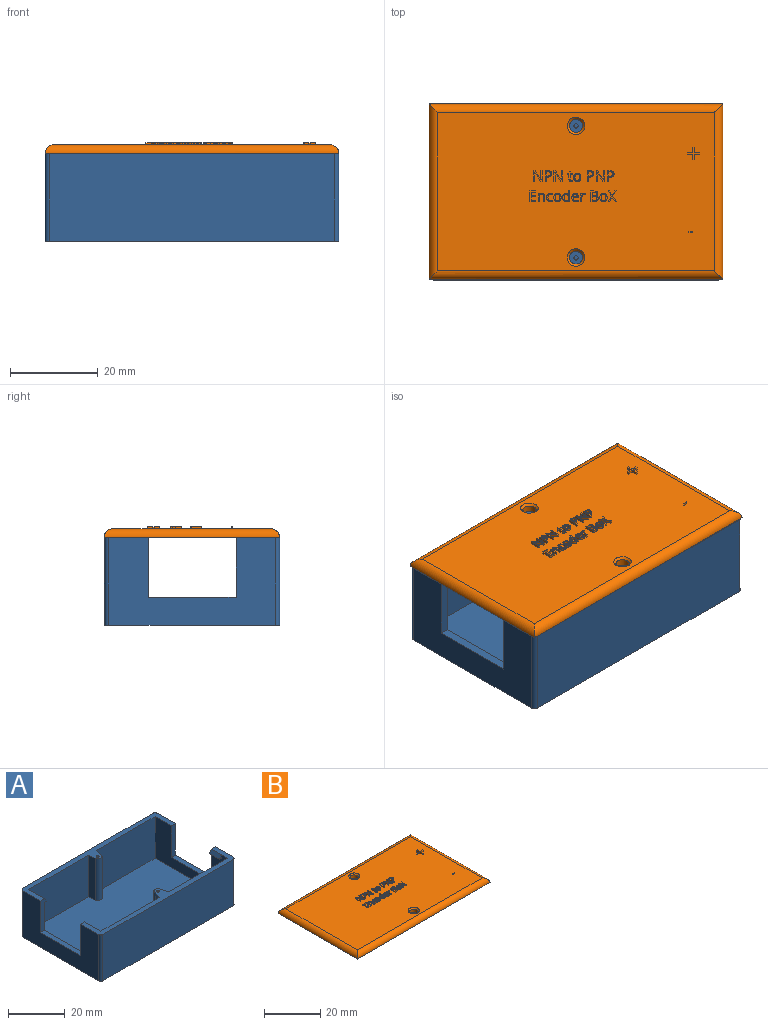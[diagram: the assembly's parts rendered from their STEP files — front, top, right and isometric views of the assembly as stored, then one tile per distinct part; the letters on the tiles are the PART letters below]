
ASSEMBLY  parts=2 mates=1
PART A: 40 faces, bbox 67x40x20 mm
  f0: plane 29.18x18mm, normal (0,1,0), area 525.2mm2, adj f1,f10,f13,f39
  f1: plane 63x36mm, normal (0,0,1), area 2239.2mm2, adj f0,f2,f3,f4,f12,f13,f14,f15
  f2: cylinder r=1.5mm len=18mm, axis (0,0,-1), area 78.3mm2, adj f1,f10,f38,f39
  f3: plane 29.36x18mm, normal (0,-1,0), area 528.4mm2, adj f1,f6,f13,f37
  f4: cylinder r=1.5mm len=18mm, axis (0,0,-1), area 76.6mm2, adj f1,f6,f36,f37
  f5: plane 38x20mm, normal (1,0,0), area 487.5mm2, adj f6,f10,f11,f19,f20,f21,f33,f34
  f6: plane 67x10mm, normal (0,0,1), area 178.5mm2, adj f3,f4,f5,f7,f9,f13,f14,f15
  f7: plane 38x20mm, normal (-1,0,0), area 487.5mm2, adj f6,f10,f11,f16,f17,f18,f32,f35
  f8: plane 65x20mm, normal (0,-1,0), area 1300mm2, adj f10,f11,f32,f33
  f9: plane 65x20mm, normal (0,1,0), area 1300mm2, adj f6,f11,f34,f35
  f10: plane 67x10mm, normal (0,0,1), area 179.9mm2, adj f0,f2,f5,f7,f8,f12,f13,f15
  f11: plane 67x40mm, normal (0,0,-1), area 2679.1mm2, adj f5,f7,f8,f9,f32,f33,f34,f35
  f12: plane 29.16x18mm, normal (0,1,0), area 524.8mm2, adj f1,f10,f15,f38
  f13: plane 36x18mm, normal (-1,0,0), area 368mm2, adj f0,f1,f3,f6,f10,f19,f20,f21
  f14: plane 29.71x18mm, normal (0,-1,0), area 534.7mm2, adj f1,f6,f15,f36
  f15: plane 36x18mm, normal (1,0,0), area 368mm2, adj f1,f6,f10,f12,f14,f16,f17,f18
  f16: plane 13.63x3mm, normal (0,-1,0), area 28mm2, adj f6,f7,f15,f17,f26,f27
  f17: plane 20x2mm, normal (0,0,1), area 40mm2, adj f7,f15,f16,f18
  f18: plane 13.63x2mm, normal (0,1,0), area 27.3mm2, adj f7,f10,f15,f17
  f19: plane 13.63x3mm, normal (0,1,0), area 28mm2, adj f5,f10,f13,f20,f29,f30
  f20: plane 20x2mm, normal (0,0,1), area 40mm2, adj f5,f13,f19,f21
  f21: plane 13.63x2mm, normal (0,-1,0), area 27.3mm2, adj f5,f6,f13,f20
  f22: cylinder r=0.5mm len=4mm, axis (0,0,1), area 12.6mm2, adj f10,f23
  f23: plane 1x1mm, normal (0,0,1), area 0.8mm2, adj f22
  f24: cylinder r=0.5mm len=4mm, axis (0,0,1), area 12.6mm2, adj f6,f25
  f25: plane 1x1mm, normal (0,0,1), area 0.8mm2, adj f24
  f26: plane 5x1mm, normal (0,0,-1), area 5mm2, adj f15,f16,f27,f28
  f27: plane 5x1.5mm, normal (0.83,0,0.55), area 9mm2, adj f6,f16,f26,f28
  f28: plane 1.5x1mm, normal (0,1,0), area 0.8mm2, adj f15,f26,f27
  f29: plane 5x1mm, normal (0,0,-1), area 5mm2, adj f13,f19,f30,f31
  f30: plane 5x1.5mm, normal (-0.83,0,0.55), area 9mm2, adj f10,f19,f29,f31
  f31: plane 1.5x1mm, normal (0,-1,0), area 0.8mm2, adj f13,f29,f30
  f32: cylinder r=1mm len=20mm, axis (0,0,1), area 31.4mm2, adj f7,f8,f10,f11
  f33: cylinder r=1mm len=20mm, axis (0,0,-1), area 31.4mm2, adj f5,f8,f10,f11
  f34: cylinder r=1mm len=20mm, axis (0,0,1), area 31.4mm2, adj f5,f6,f9,f11
  f35: cylinder r=1mm len=20mm, axis (0,0,-1), area 31.4mm2, adj f6,f7,f9,f11
  f36: plane 18x3.06mm, normal (-1,-0.1,0), area 55.4mm2, adj f1,f4,f6,f14
  f37: plane 18x3.22mm, normal (0.98,-0.21,0), area 59.3mm2, adj f1,f3,f4,f6
  f38: plane 18x2.99mm, normal (-0.96,0.27,0), area 55.8mm2, adj f1,f2,f10,f12
  f39: plane 18x3.38mm, normal (0.97,0.25,0), area 62.8mm2, adj f0,f1,f2,f10
PART B: 353 faces, bbox 67x40x2.5 mm
  f0: plane 63x36mm, normal (0,0,1), area 2205.7mm2, adj f4,f5,f6,f7,f8,f9,f10,f11
  f1: cylinder r=1.5mm len=3mm, axis (0,0,-1), area 14.1mm2, adj f3,f9
  f2: cylinder r=1.5mm len=3mm, axis (0,0,-1), area 14.1mm2, adj f3,f8
  f3: plane 67x40mm, normal (0,0,-1), area 2665.9mm2, adj f1,f2,f4,f5,f6,f7
  f4: cylinder r=2mm len=67mm, axis (1,0,0), area 205.9mm2, adj f0,f3,f5,f6
  f5: cylinder r=2mm len=40mm, axis (0,1,0), area 121.1mm2, adj f0,f3,f4,f7
  f6: cylinder r=2mm len=40mm, axis (0,-1,0), area 121.1mm2, adj f0,f3,f4,f7
  f7: cylinder r=2mm len=67mm, axis (-1,0,0), area 205.9mm2, adj f0,f3,f5,f6
  f8: cone r=1.5mm half-angle=45deg, axis (0,0,1), area 7.8mm2, adj f0,f2
  f9: cone r=1.5mm half-angle=45deg, axis (0,0,1), area 7.8mm2, adj f0,f1
  f10: plane 1.19x0.5mm, normal (0,1,0), area 0.6mm2, adj f0,f11,f21,f22
  f11: plane 1.24x0.5mm, normal (1,0,0), area 0.6mm2, adj f0,f10,f12,f22
  f12: plane 0.5x0.4mm, normal (0,1,0), area 0.2mm2, adj f0,f11,f13,f22
  f13: plane 1.24x0.5mm, normal (-1,0,0), area 0.6mm2, adj f0,f12,f14,f22
  f14: plane 1.19x0.5mm, normal (0,1,0), area 0.6mm2, adj f0,f13,f15,f22
  f15: plane 0.5x0.4mm, normal (-1,0,0), area 0.2mm2, adj f0,f14,f16,f22
  f16: plane 1.19x0.5mm, normal (0,-1,0), area 0.6mm2, adj f0,f15,f17,f22
  f17: plane 1.23x0.5mm, normal (-1,0,0), area 0.6mm2, adj f0,f16,f18,f22
  f18: plane 0.5x0.4mm, normal (0,-1,0), area 0.2mm2, adj f0,f17,f19,f22
  f19: plane 1.23x0.5mm, normal (1,0,0), area 0.6mm2, adj f0,f18,f20,f22
  f20: plane 1.19x0.5mm, normal (0,-1,0), area 0.6mm2, adj f0,f19,f21,f22
  f21: plane 0.5x0.4mm, normal (1,0,0), area 0.2mm2, adj f0,f10,f20,f22
  f22: plane 2.87x2.78mm, normal (0,0,1), area 2.1mm2, adj f10,f11,f12,f13,f14,f15,f16,f17
  f23: plane 0.5x0.32mm, normal (0,-1,0), area 0.2mm2, adj f0,f24,f37,f38
  f24: plane 2.42x0.5mm, normal (1,0,0), area 1.2mm2, adj f0,f23,f25,f38
  f25: plane 0.5x0.26mm, normal (0,1,0), area 0.1mm2, adj f0,f24,f26,f38
  f26: plane 1.39x0.5mm, normal (-1,0,0), area 0.7mm2, adj f0,f25,f27,f38
  f27: extruded ~0.5x0.35mm, area 0.2mm2, adj f0,f26,f28,f38
  f28: extruded ~0.5x0.29mm, area 0.1mm2, adj f0,f27,f29,f38
  f29: plane 0.5x0.01mm, normal (0,1,0), area 0mm2, adj f0,f28,f30,f38
  f30: plane 2.02x1.32mm, normal (0.84,0.55,0), area 1.2mm2, adj f0,f29,f31,f38
  f31: plane 0.5x0.32mm, normal (0,1,0), area 0.2mm2, adj f0,f30,f32,f38
  f32: plane 2.42x0.5mm, normal (-1,0,0), area 1.2mm2, adj f0,f31,f33,f38
  f33: plane 0.5x0.26mm, normal (0,-1,0), area 0.1mm2, adj f0,f32,f34,f38
  f34: plane 1.38x0.5mm, normal (1,0,0), area 0.7mm2, adj f0,f33,f35,f38
  f35: extruded ~0.66x0.5mm, area 0.3mm2, adj f0,f34,f36,f38
  f36: plane 0.5x0.01mm, normal (0,-1,0), area 0mm2, adj f0,f35,f37,f38
  f37: plane 2.03x1.32mm, normal (-0.84,-0.55,0), area 1.2mm2, adj f0,f23,f36,f38
  f38: plane 2.42x1.89mm, normal (0,0,1), area 1.9mm2, adj f23,f24,f25,f26,f27,f28,f29,f30
  f39: plane 0.5x0.25mm, normal (0,1,0), area 0.1mm2, adj f40,f53,f54,f55
  f40: plane 0.98x0.5mm, normal (1,0,0), area 0.5mm2, adj f39,f41,f54,f55
  f41: plane 0.5x0.31mm, normal (0,-1,0), area 0.2mm2, adj f40,f42,f54,f55
  f42: extruded ~0.5x0.49mm, area 0.3mm2, adj f41,f43,f54,f55
  f43: extruded ~0.5x0.36mm, area 0.2mm2, adj f42,f44,f54,f55
  f44: extruded ~0.5x0.39mm, area 0.2mm2, adj f43,f53,f54,f55
  f45: extruded ~0.57x0.5mm, area 0.3mm2, adj f0,f46,f52,f54
  f46: extruded ~0.91x0.71mm, area 0.7mm2, adj f0,f45,f47,f54
  f47: plane 0.63x0.5mm, normal (0,1,0), area 0.3mm2, adj f0,f46,f48,f54
  f48: plane 2.42x0.5mm, normal (-1,0,0), area 1.2mm2, adj f0,f47,f49,f54
  f49: plane 0.5x0.28mm, normal (0,-1,0), area 0.1mm2, adj f0,f48,f50,f54
  f50: plane 0.95x0.5mm, normal (1,0,0), area 0.5mm2, adj f0,f49,f51,f54
  f51: plane 0.5x0.29mm, normal (0,-1,0), area 0.1mm2, adj f0,f50,f52,f54
  f52: extruded ~0.72x0.5mm, area 0.4mm2, adj f0,f45,f51,f54
  f53: extruded ~0.54x0.5mm, area 0.3mm2, adj f39,f44,f54,f55
  f54: plane 2.42x1.53mm, normal (0,0,1), area 1.4mm2, adj f39,f40,f41,f42,f43,f44,f45,f46
  f55: plane 0.98x0.96mm, normal (0,0,1), area 0.8mm2, adj f39,f40,f41,f42,f43,f44,f53
  f56: plane 0.5x0.32mm, normal (0,-1,0), area 0.2mm2, adj f0,f57,f70,f71
  f57: plane 2.42x0.5mm, normal (1,0,0), area 1.2mm2, adj f0,f56,f58,f71
  f58: plane 0.5x0.26mm, normal (0,1,0), area 0.1mm2, adj f0,f57,f59,f71
  f59: plane 1.39x0.5mm, normal (-1,0,0), area 0.7mm2, adj f0,f58,f60,f71
  f60: extruded ~0.5x0.35mm, area 0.2mm2, adj f0,f59,f61,f71
  f61: extruded ~0.5x0.29mm, area 0.1mm2, adj f0,f60,f62,f71
  f62: plane 0.5x0.01mm, normal (0,1,0), area 0mm2, adj f0,f61,f63,f71
  f63: plane 2.02x1.32mm, normal (0.84,0.55,0), area 1.2mm2, adj f0,f62,f64,f71
  f64: plane 0.5x0.32mm, normal (0,1,0), area 0.2mm2, adj f0,f63,f65,f71
  f65: plane 2.42x0.5mm, normal (-1,0,0), area 1.2mm2, adj f0,f64,f66,f71
  f66: plane 0.5x0.26mm, normal (0,-1,0), area 0.1mm2, adj f0,f65,f67,f71
  f67: plane 1.38x0.5mm, normal (1,0,0), area 0.7mm2, adj f0,f66,f68,f71
  f68: extruded ~0.66x0.5mm, area 0.3mm2, adj f0,f67,f69,f71
  f69: plane 0.5x0.01mm, normal (0,-1,0), area 0mm2, adj f0,f68,f70,f71
  f70: plane 2.03x1.32mm, normal (-0.84,-0.55,0), area 1.2mm2, adj f0,f56,f69,f71
  f71: plane 2.42x1.89mm, normal (0,0,1), area 1.9mm2, adj f56,f57,f58,f59,f60,f61,f62,f63
  f72: extruded ~0.5x0.14mm, area 0.1mm2, adj f0,f73,f90,f91
  f73: extruded ~0.5x0.21mm, area 0.1mm2, adj f0,f72,f74,f91
  f74: extruded ~0.5x0.25mm, area 0.1mm2, adj f0,f73,f75,f91
  f75: plane 1.07x0.5mm, normal (1,0,0), area 0.5mm2, adj f0,f74,f76,f91
  f76: plane 0.53x0.5mm, normal (0,-1,0), area 0.3mm2, adj f0,f75,f77,f91
  f77: plane 0.5x0.21mm, normal (1,0,0), area 0.1mm2, adj f0,f76,f78,f91
  f78: plane 0.53x0.5mm, normal (0,1,0), area 0.3mm2, adj f0,f77,f79,f91
  f79: plane 0.5x0.42mm, normal (1,0,0), area 0.2mm2, adj f0,f78,f80,f91
  f80: plane 0.5x0.16mm, normal (0,1,0), area 0.1mm2, adj f0,f79,f81,f91
  f81: plane 0.5x0.39mm, normal (-0.96,0.29,0), area 0.2mm2, adj f0,f80,f82,f91
  f82: plane 0.5x0.26mm, normal (-0.4,0.92,0), area 0.1mm2, adj f0,f81,f83,f91
  f83: plane 0.5x0.13mm, normal (-1,0,0), area 0.1mm2, adj f0,f82,f84,f91
  f84: plane 0.5x0.26mm, normal (0,-1,0), area 0.1mm2, adj f0,f83,f85,f91
  f85: plane 1.08x0.5mm, normal (-1,0,0), area 0.5mm2, adj f0,f84,f86,f91
  f86: extruded ~0.55x0.53mm, area 0.4mm2, adj f0,f85,f87,f91
  f87: extruded ~0.5x0.16mm, area 0.1mm2, adj f0,f86,f88,f91
  f88: extruded ~0.5x0.13mm, area 0.1mm2, adj f0,f87,f89,f91
  f89: plane 0.5x0.21mm, normal (1,0,0), area 0.1mm2, adj f0,f88,f90,f91
  f90: extruded ~0.5x0.11mm, area 0.1mm2, adj f0,f72,f89,f91
  f91: plane 2.27x1.07mm, normal (0,0,1), area 0.9mm2, adj f72,f73,f74,f75,f76,f77,f78,f79
  f92: extruded ~0.53x0.5mm, area 0.3mm2, adj f93,f108,f109,f110
  f93: extruded ~0.53x0.5mm, area 0.3mm2, adj f92,f94,f109,f110
  f94: extruded ~0.5x0.41mm, area 0.2mm2, adj f93,f95,f109,f110
  f95: extruded ~0.5x0.41mm, area 0.2mm2, adj f94,f96,f109,f110
  f96: extruded ~0.53x0.5mm, area 0.3mm2, adj f95,f97,f109,f110
  f97: extruded ~0.53x0.5mm, area 0.3mm2, adj f96,f98,f109,f110
  f98: extruded ~0.5x0.41mm, area 0.2mm2, adj f97,f108,f109,f110
  f99: extruded ~0.69x0.5mm, area 0.4mm2, adj f0,f100,f107,f109
  f100: extruded ~0.69x0.5mm, area 0.4mm2, adj f0,f99,f101,f109
  f101: extruded ~0.6x0.5mm, area 0.3mm2, adj f0,f100,f102,f109
  f102: extruded ~0.62x0.5mm, area 0.3mm2, adj f0,f101,f103,f109
  f103: extruded ~0.69x0.5mm, area 0.4mm2, adj f0,f102,f104,f109
  f104: extruded ~0.5x0.5mm, area 0.3mm2, adj f0,f103,f105,f109
  f105: extruded ~0.5x0.33mm, area 0.2mm2, adj f0,f104,f106,f109
  f106: extruded ~0.5x0.43mm, area 0.2mm2, adj f0,f105,f107,f109
  f107: extruded ~0.62x0.5mm, area 0.3mm2, adj f0,f99,f106,f109
  f108: extruded ~0.5x0.41mm, area 0.2mm2, adj f92,f98,f109,f110
  f109: plane 1.88x1.67mm, normal (0,0,1), area 1.3mm2, adj f92,f93,f94,f95,f96,f97,f98,f99
  f110: plane 1.42x1.1mm, normal (0,0,1), area 1.3mm2, adj f92,f93,f94,f95,f96,f97,f98,f108
  f111: plane 0.5x0.25mm, normal (0,1,0), area 0.1mm2, adj f112,f125,f126,f127
  f112: plane 0.98x0.5mm, normal (1,0,0), area 0.5mm2, adj f111,f113,f126,f127
  f113: plane 0.5x0.31mm, normal (0,-1,0), area 0.2mm2, adj f112,f114,f126,f127
  f114: extruded ~0.5x0.49mm, area 0.3mm2, adj f113,f115,f126,f127
  f115: extruded ~0.5x0.36mm, area 0.2mm2, adj f114,f116,f126,f127
  f116: extruded ~0.5x0.39mm, area 0.2mm2, adj f115,f125,f126,f127
  f117: extruded ~0.57x0.5mm, area 0.3mm2, adj f0,f118,f124,f126
  f118: extruded ~0.91x0.71mm, area 0.7mm2, adj f0,f117,f119,f126
  f119: plane 0.63x0.5mm, normal (0,1,0), area 0.3mm2, adj f0,f118,f120,f126
  f120: plane 2.42x0.5mm, normal (-1,0,0), area 1.2mm2, adj f0,f119,f121,f126
  f121: plane 0.5x0.28mm, normal (0,-1,0), area 0.1mm2, adj f0,f120,f122,f126
  f122: plane 0.95x0.5mm, normal (1,0,0), area 0.5mm2, adj f0,f121,f123,f126
  f123: plane 0.5x0.29mm, normal (0,-1,0), area 0.1mm2, adj f0,f122,f124,f126
  f124: extruded ~0.72x0.5mm, area 0.4mm2, adj f0,f117,f123,f126
  f125: extruded ~0.54x0.5mm, area 0.3mm2, adj f111,f116,f126,f127
  f126: plane 2.42x1.53mm, normal (0,0,1), area 1.4mm2, adj f111,f112,f113,f114,f115,f116,f117,f118
  f127: plane 0.98x0.96mm, normal (0,0,1), area 0.8mm2, adj f111,f112,f113,f114,f115,f116,f125
  f128: plane 0.5x0.32mm, normal (0,-1,0), area 0.2mm2, adj f0,f129,f142,f143
  f129: plane 2.42x0.5mm, normal (1,0,0), area 1.2mm2, adj f0,f128,f130,f143
  f130: plane 0.5x0.26mm, normal (0,1,0), area 0.1mm2, adj f0,f129,f131,f143
  f131: plane 1.39x0.5mm, normal (-1,0,0), area 0.7mm2, adj f0,f130,f132,f143
  f132: extruded ~0.5x0.35mm, area 0.2mm2, adj f0,f131,f133,f143
  f133: extruded ~0.5x0.29mm, area 0.1mm2, adj f0,f132,f134,f143
  f134: plane 0.5x0.01mm, normal (0,1,0), area 0mm2, adj f0,f133,f135,f143
  f135: plane 2.02x1.32mm, normal (0.84,0.55,0), area 1.2mm2, adj f0,f134,f136,f143
  f136: plane 0.5x0.32mm, normal (0,1,0), area 0.2mm2, adj f0,f135,f137,f143
  f137: plane 2.42x0.5mm, normal (-1,0,0), area 1.2mm2, adj f0,f136,f138,f143
  f138: plane 0.5x0.26mm, normal (0,-1,0), area 0.1mm2, adj f0,f137,f139,f143
  f139: plane 1.38x0.5mm, normal (1,0,0), area 0.7mm2, adj f0,f138,f140,f143
  f140: extruded ~0.66x0.5mm, area 0.3mm2, adj f0,f139,f141,f143
  f141: plane 0.5x0.01mm, normal (0,-1,0), area 0mm2, adj f0,f140,f142,f143
  f142: plane 2.03x1.32mm, normal (-0.84,-0.55,0), area 1.2mm2, adj f0,f128,f141,f143
  f143: plane 2.42x1.89mm, normal (0,0,1), area 1.9mm2, adj f128,f129,f130,f131,f132,f133,f134,f135
  f144: plane 0.5x0.25mm, normal (0,1,0), area 0.1mm2, adj f145,f158,f159,f160
  f145: plane 0.98x0.5mm, normal (1,0,0), area 0.5mm2, adj f144,f146,f159,f160
  f146: plane 0.5x0.31mm, normal (0,-1,0), area 0.2mm2, adj f145,f147,f159,f160
  f147: extruded ~0.5x0.49mm, area 0.3mm2, adj f146,f148,f159,f160
  f148: extruded ~0.5x0.36mm, area 0.2mm2, adj f147,f149,f159,f160
  f149: extruded ~0.5x0.39mm, area 0.2mm2, adj f148,f158,f159,f160
  f150: extruded ~0.57x0.5mm, area 0.3mm2, adj f0,f151,f157,f159
  f151: extruded ~0.91x0.71mm, area 0.7mm2, adj f0,f150,f152,f159
  f152: plane 0.63x0.5mm, normal (0,1,0), area 0.3mm2, adj f0,f151,f153,f159
  f153: plane 2.42x0.5mm, normal (-1,0,0), area 1.2mm2, adj f0,f152,f154,f159
  f154: plane 0.5x0.28mm, normal (0,-1,0), area 0.1mm2, adj f0,f153,f155,f159
  f155: plane 0.95x0.5mm, normal (1,0,0), area 0.5mm2, adj f0,f154,f156,f159
  f156: plane 0.5x0.29mm, normal (0,-1,0), area 0.1mm2, adj f0,f155,f157,f159
  f157: extruded ~0.72x0.5mm, area 0.4mm2, adj f0,f150,f156,f159
  f158: extruded ~0.54x0.5mm, area 0.3mm2, adj f144,f149,f159,f160
  f159: plane 2.42x1.53mm, normal (0,0,1), area 1.4mm2, adj f144,f145,f146,f147,f148,f149,f150,f151
  f160: plane 0.98x0.96mm, normal (0,0,1), area 0.8mm2, adj f144,f145,f146,f147,f148,f149,f158
  f161: plane 1.35x0.5mm, normal (0,-1,0), area 0.7mm2, adj f0,f162,f172,f173
  f162: plane 0.5x0.25mm, normal (1,0,0), area 0.1mm2, adj f0,f161,f163,f173
  f163: plane 1.07x0.5mm, normal (0,1,0), area 0.5mm2, adj f0,f162,f164,f173
  f164: plane 0.89x0.5mm, normal (1,0,0), area 0.4mm2, adj f0,f163,f165,f173
  f165: plane 1x0.5mm, normal (0,-1,0), area 0.5mm2, adj f0,f164,f166,f173
  f166: plane 0.5x0.25mm, normal (1,0,0), area 0.1mm2, adj f0,f165,f167,f173
  f167: plane 1x0.5mm, normal (0,1,0), area 0.5mm2, adj f0,f166,f168,f173
  f168: plane 0.78x0.5mm, normal (1,0,0), area 0.4mm2, adj f0,f167,f169,f173
  f169: plane 1.07x0.5mm, normal (0,-1,0), area 0.5mm2, adj f0,f168,f170,f173
  f170: plane 0.5x0.25mm, normal (1,0,0), area 0.1mm2, adj f0,f169,f171,f173
  f171: plane 1.35x0.5mm, normal (0,1,0), area 0.7mm2, adj f0,f170,f172,f173
  f172: plane 2.42x0.5mm, normal (-1,0,0), area 1.2mm2, adj f0,f161,f171,f173
  f173: plane 2.42x1.35mm, normal (0,0,1), area 1.5mm2, adj f161,f162,f163,f164,f165,f166,f167,f168
  f174: plane 1.17x0.5mm, normal (-1,0,0), area 0.6mm2, adj f0,f175,f190,f191
  f175: plane 0.5x0.28mm, normal (0,-1,0), area 0.1mm2, adj f0,f174,f176,f191
  f176: plane 1.18x0.5mm, normal (1,0,0), area 0.6mm2, adj f0,f175,f177,f191
  f177: extruded ~0.51x0.5mm, area 0.3mm2, adj f0,f176,f178,f191
  f178: extruded ~0.5x0.49mm, area 0.3mm2, adj f0,f177,f179,f191
  f179: extruded ~0.5x0.34mm, area 0.2mm2, adj f0,f178,f180,f191
  f180: extruded ~0.5x0.24mm, area 0.2mm2, adj f0,f179,f181,f191
  f181: plane 0.5x0.01mm, normal (0,1,0), area 0mm2, adj f0,f180,f182,f191
  f182: plane 0.5x0.25mm, normal (0.98,0.18,0), area 0.1mm2, adj f0,f181,f183,f191
  f183: plane 0.5x0.22mm, normal (0,1,0), area 0.1mm2, adj f0,f182,f184,f191
  f184: plane 1.81x0.5mm, normal (-1,0,0), area 0.9mm2, adj f0,f183,f185,f191
  f185: plane 0.5x0.28mm, normal (0,-1,0), area 0.1mm2, adj f0,f184,f186,f191
  f186: plane 0.95x0.5mm, normal (1,0,0), area 0.5mm2, adj f0,f185,f187,f191
  f187: extruded ~0.51x0.5mm, area 0.3mm2, adj f0,f186,f188,f191
  f188: extruded ~0.5x0.42mm, area 0.2mm2, adj f0,f187,f189,f191
  f189: extruded ~0.5x0.32mm, area 0.2mm2, adj f0,f188,f190,f191
  f190: extruded ~0.5x0.33mm, area 0.2mm2, adj f0,f174,f189,f191
  f191: plane 1.85x1.52mm, normal (0,0,1), area 1.2mm2, adj f174,f175,f176,f177,f178,f179,f180,f181
  f192: extruded ~0.61x0.5mm, area 0.3mm2, adj f0,f193,f206,f207
  f193: extruded ~0.5x0.46mm, area 0.2mm2, adj f0,f192,f194,f207
  f194: plane 0.5x0.24mm, normal (1,0,0), area 0.1mm2, adj f0,f193,f195,f207
  f195: extruded ~0.5x0.47mm, area 0.2mm2, adj f0,f194,f196,f207
  f196: extruded ~0.5x0.4mm, area 0.2mm2, adj f0,f195,f197,f207
  f197: extruded ~0.51x0.5mm, area 0.3mm2, adj f0,f196,f198,f207
  f198: extruded ~0.71x0.55mm, area 0.5mm2, adj f0,f197,f199,f207
  f199: extruded ~0.5x0.19mm, area 0.1mm2, adj f0,f198,f200,f207
  f200: extruded ~0.5x0.2mm, area 0.1mm2, adj f0,f199,f201,f207
  f201: plane 0.5x0.23mm, normal (0.94,-0.34,0), area 0.1mm2, adj f0,f200,f202,f207
  f202: extruded ~0.5x0.21mm, area 0.1mm2, adj f0,f201,f203,f207
  f203: extruded ~0.5x0.26mm, area 0.1mm2, adj f0,f202,f204,f207
  f204: extruded ~0.62x0.5mm, area 0.3mm2, adj f0,f203,f205,f207
  f205: extruded ~0.7x0.5mm, area 0.4mm2, adj f0,f204,f206,f207
  f206: extruded ~0.69x0.5mm, area 0.4mm2, adj f0,f192,f205,f207
  f207: plane 1.88x1.31mm, normal (0,0,1), area 0.9mm2, adj f192,f193,f194,f195,f196,f197,f198,f199
  f208: extruded ~0.53x0.5mm, area 0.3mm2, adj f209,f224,f225,f226
  f209: extruded ~0.53x0.5mm, area 0.3mm2, adj f208,f210,f225,f226
  f210: extruded ~0.5x0.41mm, area 0.2mm2, adj f209,f211,f225,f226
  f211: extruded ~0.5x0.41mm, area 0.2mm2, adj f210,f212,f225,f226
  f212: extruded ~0.53x0.5mm, area 0.3mm2, adj f211,f213,f225,f226
  f213: extruded ~0.53x0.5mm, area 0.3mm2, adj f212,f214,f225,f226
  f214: extruded ~0.5x0.41mm, area 0.2mm2, adj f213,f224,f225,f226
  f215: extruded ~0.69x0.5mm, area 0.4mm2, adj f0,f216,f223,f225
  f216: extruded ~0.69x0.5mm, area 0.4mm2, adj f0,f215,f217,f225
  f217: extruded ~0.6x0.5mm, area 0.3mm2, adj f0,f216,f218,f225
  f218: extruded ~0.62x0.5mm, area 0.3mm2, adj f0,f217,f219,f225
  f219: extruded ~0.69x0.5mm, area 0.4mm2, adj f0,f218,f220,f225
  f220: extruded ~0.5x0.5mm, area 0.3mm2, adj f0,f219,f221,f225
  f221: extruded ~0.5x0.33mm, area 0.2mm2, adj f0,f220,f222,f225
  f222: extruded ~0.5x0.43mm, area 0.2mm2, adj f0,f221,f223,f225
  f223: extruded ~0.62x0.5mm, area 0.3mm2, adj f0,f215,f222,f225
  f224: extruded ~0.5x0.41mm, area 0.2mm2, adj f208,f214,f225,f226
  f225: plane 1.88x1.67mm, normal (0,0,1), area 1.3mm2, adj f208,f209,f210,f211,f212,f213,f214,f215
  f226: plane 1.42x1.1mm, normal (0,0,1), area 1.3mm2, adj f208,f209,f210,f211,f212,f213,f214,f224
  f227: extruded ~0.5x0.41mm, area 0.2mm2, adj f228,f250,f251,f252
  f228: extruded ~0.5x0.37mm, area 0.2mm2, adj f227,f229,f251,f252
  f229: extruded ~0.52x0.5mm, area 0.3mm2, adj f228,f230,f251,f252
  f230: extruded ~0.53x0.5mm, area 0.3mm2, adj f229,f231,f251,f252
  f231: extruded ~0.5x0.37mm, area 0.2mm2, adj f230,f232,f251,f252
  f232: extruded ~0.5x0.41mm, area 0.2mm2, adj f231,f233,f251,f252
  f233: extruded ~0.55x0.5mm, area 0.3mm2, adj f232,f234,f251,f252
  f234: plane 0.5x0.06mm, normal (-1,0,0), area 0mm2, adj f233,f250,f251,f252
  f235: plane 0.5x0.02mm, normal (0,-1,0), area 0mm2, adj f0,f236,f249,f251
  f236: plane 0.5x0.24mm, normal (-0.99,-0.15,0), area 0.1mm2, adj f0,f235,f237,f251
  f237: plane 0.5x0.22mm, normal (0,-1,0), area 0.1mm2, adj f0,f236,f238,f251
  f238: plane 2.58x0.5mm, normal (1,0,0), area 1.3mm2, adj f0,f237,f239,f251
  f239: plane 0.5x0.28mm, normal (0,1,0), area 0.1mm2, adj f0,f238,f240,f251
  f240: plane 0.74x0.5mm, normal (-1,0,0), area 0.4mm2, adj f0,f239,f241,f251
  f241: plane 0.5x0.13mm, normal (-1,-0.05,0), area 0.1mm2, adj f0,f240,f242,f251
  f242: plane 0.5x0.13mm, normal (-1,-0.09,0), area 0.1mm2, adj f0,f241,f243,f251
  f243: plane 0.5x0.02mm, normal (0,1,0), area 0mm2, adj f0,f242,f244,f251
  f244: extruded ~0.57x0.5mm, area 0.3mm2, adj f0,f243,f245,f251
  f245: extruded ~0.55x0.5mm, area 0.3mm2, adj f0,f244,f246,f251
  f246: extruded ~0.7x0.5mm, area 0.4mm2, adj f0,f245,f247,f251
  f247: extruded ~0.69x0.5mm, area 0.4mm2, adj f0,f246,f248,f251
  f248: extruded ~0.55x0.5mm, area 0.3mm2, adj f0,f247,f249,f251
  f249: extruded ~0.57x0.5mm, area 0.3mm2, adj f0,f235,f248,f251
  f250: extruded ~0.5x0.49mm, area 0.3mm2, adj f227,f234,f251,f252
  f251: plane 2.61x1.6mm, normal (0,0,1), area 1.6mm2, adj f227,f228,f229,f230,f231,f232,f233,f234
  f252: plane 1.42x1.04mm, normal (0,0,1), area 1.2mm2, adj f227,f228,f229,f230,f231,f232,f233,f234
  f253: extruded ~0.5x0.35mm, area 0.2mm2, adj f254,f271,f272,f273
  f254: extruded ~0.5x0.33mm, area 0.2mm2, adj f253,f255,f272,f273
  f255: extruded ~0.5x0.4mm, area 0.2mm2, adj f254,f256,f272,f273
  f256: plane 0.95x0.5mm, normal (0,1,0), area 0.5mm2, adj f255,f271,f272,f273
  f257: extruded ~0.63x0.5mm, area 0.4mm2, adj f0,f258,f270,f272
  f258: extruded ~0.5x0.31mm, area 0.2mm2, adj f0,f257,f259,f272
  f259: extruded ~0.5x0.28mm, area 0.1mm2, adj f0,f258,f260,f272
  f260: plane 0.5x0.25mm, normal (1,0,0), area 0.1mm2, adj f0,f259,f261,f272
  f261: extruded ~0.58x0.5mm, area 0.3mm2, adj f0,f260,f262,f272
  f262: extruded ~0.5x0.43mm, area 0.2mm2, adj f0,f261,f263,f272
  f263: extruded ~0.5x0.49mm, area 0.3mm2, adj f0,f262,f264,f272
  f264: plane 1.25x0.5mm, normal (0,-1,0), area 0.6mm2, adj f0,f263,f265,f272
  f265: plane 0.5x0.17mm, normal (1,0,0), area 0.1mm2, adj f0,f264,f266,f272
  f266: extruded ~0.59x0.5mm, area 0.3mm2, adj f0,f265,f267,f272
  f267: extruded ~0.54x0.5mm, area 0.3mm2, adj f0,f266,f268,f272
  f268: extruded ~0.58x0.5mm, area 0.3mm2, adj f0,f267,f269,f272
  f269: extruded ~0.7x0.5mm, area 0.4mm2, adj f0,f268,f270,f272
  f270: extruded ~0.68x0.5mm, area 0.4mm2, adj f0,f257,f269,f272
  f271: extruded ~0.5x0.39mm, area 0.2mm2, adj f253,f256,f272,f273
  f272: plane 1.88x1.53mm, normal (0,0,1), area 1.3mm2, adj f253,f254,f255,f256,f257,f258,f259,f260
  f273: plane 0.95x0.54mm, normal (0,0,1), area 0.4mm2, adj f253,f254,f255,f256,f271
  f274: extruded ~0.5x0.22mm, area 0.1mm2, adj f0,f275,f286,f287
  f275: extruded ~0.5x0.31mm, area 0.2mm2, adj f0,f274,f276,f287
  f276: extruded ~0.5x0.27mm, area 0.2mm2, adj f0,f275,f277,f287
  f277: plane 0.5x0.01mm, normal (0,1,0), area 0mm2, adj f0,f276,f278,f287
  f278: plane 0.5x0.34mm, normal (1,0.09,0), area 0.2mm2, adj f0,f277,f279,f287
  f279: plane 0.5x0.23mm, normal (0,1,0), area 0.1mm2, adj f0,f278,f280,f287
  f280: plane 1.81x0.5mm, normal (-1,0,0), area 0.9mm2, adj f0,f279,f281,f287
  f281: plane 0.5x0.28mm, normal (0,-1,0), area 0.1mm2, adj f0,f280,f282,f287
  f282: plane 0.97x0.5mm, normal (1,0,0), area 0.5mm2, adj f0,f281,f283,f287
  f283: extruded ~0.5x0.45mm, area 0.2mm2, adj f0,f282,f284,f287
  f284: extruded ~0.5x0.38mm, area 0.2mm2, adj f0,f283,f285,f287
  f285: extruded ~0.5x0.2mm, area 0.1mm2, adj f0,f284,f286,f287
  f286: plane 0.5x0.25mm, normal (0.99,-0.15,0), area 0.1mm2, adj f0,f274,f285,f287
  f287: plane 1.85x1.04mm, normal (0,0,1), area 0.7mm2, adj f274,f275,f276,f277,f278,f279,f280,f281
  f288: plane 0.91x0.5mm, normal (1,0,0), area 0.5mm2, adj f289,f312,f313,f314
  f289: plane 0.5x0.48mm, normal (0,-1,0), area 0.2mm2, adj f288,f290,f313,f314
  f290: extruded ~0.5x0.46mm, area 0.2mm2, adj f289,f291,f313,f314
  f291: extruded ~0.5x0.33mm, area 0.2mm2, adj f290,f292,f313,f314
  f292: extruded ~0.5x0.36mm, area 0.2mm2, adj f291,f293,f313,f314
  f293: extruded ~0.5x0.44mm, area 0.2mm2, adj f292,f312,f313,f314
  f294: plane 0.5x0.46mm, normal (0,1,0), area 0.2mm2, adj f295,f310,f313,f315
  f295: plane 0.79x0.5mm, normal (1,0,0), area 0.4mm2, adj f294,f296,f313,f315
  f296: plane 0.5x0.41mm, normal (0,-1,0), area 0.2mm2, adj f295,f297,f313,f315
  f297: extruded ~0.5x0.46mm, area 0.2mm2, adj f296,f298,f313,f315
  f298: extruded ~0.5x0.29mm, area 0.2mm2, adj f297,f299,f313,f315
  f299: extruded ~0.5x0.32mm, area 0.2mm2, adj f298,f310,f313,f315
  f300: plane 0.68x0.5mm, normal (0,1,0), area 0.3mm2, adj f0,f301,f311,f313
  f301: plane 2.42x0.5mm, normal (-1,0,0), area 1.2mm2, adj f0,f300,f302,f313
  f302: plane 0.84x0.5mm, normal (0,-1,0), area 0.4mm2, adj f0,f301,f303,f313
  f303: extruded ~0.61x0.5mm, area 0.3mm2, adj f0,f302,f304,f313
  f304: extruded ~0.51x0.5mm, area 0.3mm2, adj f0,f303,f305,f313
  f305: extruded ~0.58x0.55mm, area 0.4mm2, adj f0,f304,f306,f313
  f306: plane 0.5x0.02mm, normal (1,0,0), area 0mm2, adj f0,f305,f307,f313
  f307: extruded ~0.5x0.35mm, area 0.2mm2, adj f0,f306,f308,f313
  f308: extruded ~0.5x0.36mm, area 0.2mm2, adj f0,f307,f309,f313
  f309: extruded ~0.5x0.46mm, area 0.3mm2, adj f0,f308,f311,f313
  f310: extruded ~0.5x0.43mm, area 0.2mm2, adj f294,f299,f313,f315
  f311: extruded ~0.7x0.5mm, area 0.4mm2, adj f0,f300,f309,f313
  f312: plane 0.51x0.5mm, normal (0,1,0), area 0.3mm2, adj f288,f293,f313,f314
  f313: plane 2.42x1.68mm, normal (0,0,1), area 2mm2, adj f288,f289,f290,f291,f292,f293,f294,f295
  f314: plane 1.09x0.91mm, normal (0,0,1), area 0.9mm2, adj f288,f289,f290,f291,f292,f293,f312
  f315: plane 1.02x0.79mm, normal (0,0,1), area 0.7mm2, adj f294,f295,f296,f297,f298,f299,f310
  f316: extruded ~0.53x0.5mm, area 0.3mm2, adj f317,f332,f333,f334
  f317: extruded ~0.53x0.5mm, area 0.3mm2, adj f316,f318,f333,f334
  f318: extruded ~0.5x0.41mm, area 0.2mm2, adj f317,f319,f333,f334
  f319: extruded ~0.5x0.41mm, area 0.2mm2, adj f318,f320,f333,f334
  f320: extruded ~0.53x0.5mm, area 0.3mm2, adj f319,f321,f333,f334
  f321: extruded ~0.53x0.5mm, area 0.3mm2, adj f320,f322,f333,f334
  f322: extruded ~0.5x0.41mm, area 0.2mm2, adj f321,f332,f333,f334
  f323: extruded ~0.69x0.5mm, area 0.4mm2, adj f0,f324,f331,f333
  f324: extruded ~0.69x0.5mm, area 0.4mm2, adj f0,f323,f325,f333
  f325: extruded ~0.6x0.5mm, area 0.3mm2, adj f0,f324,f326,f333
  f326: extruded ~0.62x0.5mm, area 0.3mm2, adj f0,f325,f327,f333
  f327: extruded ~0.69x0.5mm, area 0.4mm2, adj f0,f326,f328,f333
  f328: extruded ~0.5x0.5mm, area 0.3mm2, adj f0,f327,f329,f333
  f329: extruded ~0.5x0.33mm, area 0.2mm2, adj f0,f328,f330,f333
  f330: extruded ~0.5x0.43mm, area 0.2mm2, adj f0,f329,f331,f333
  f331: extruded ~0.62x0.5mm, area 0.3mm2, adj f0,f323,f330,f333
  f332: extruded ~0.5x0.41mm, area 0.2mm2, adj f316,f322,f333,f334
  f333: plane 1.88x1.67mm, normal (0,0,1), area 1.3mm2, adj f316,f317,f318,f319,f320,f321,f322,f323
  f334: plane 1.42x1.1mm, normal (0,0,1), area 1.3mm2, adj f316,f317,f318,f319,f320,f321,f322,f332
  f335: plane 0.5x0.32mm, normal (0,-1,0), area 0.2mm2, adj f0,f336,f346,f347
  f336: plane 1.27x0.81mm, normal (0.84,0.54,0), area 0.8mm2, adj f0,f335,f337,f347
  f337: plane 1.15x0.75mm, normal (0.84,-0.55,0), area 0.7mm2, adj f0,f336,f338,f347
  f338: plane 0.5x0.3mm, normal (0,1,0), area 0.1mm2, adj f0,f337,f339,f347
  f339: plane 0.96x0.61mm, normal (-0.85,0.53,0), area 0.6mm2, adj f0,f338,f340,f347
  f340: plane 0.96x0.6mm, normal (0.85,0.53,0), area 0.6mm2, adj f0,f339,f341,f347
  f341: plane 0.5x0.31mm, normal (0,1,0), area 0.2mm2, adj f0,f340,f342,f347
  f342: plane 1.16x0.75mm, normal (-0.84,-0.54,0), area 0.7mm2, adj f0,f341,f343,f347
  f343: plane 1.26x0.8mm, normal (-0.84,0.54,0), area 0.7mm2, adj f0,f342,f344,f347
  f344: plane 0.5x0.3mm, normal (0,-1,0), area 0.1mm2, adj f0,f343,f345,f347
  f345: plane 1.06x0.66mm, normal (0.85,-0.53,0), area 0.6mm2, adj f0,f344,f346,f347
  f346: plane 1.06x0.65mm, normal (-0.85,-0.52,0), area 0.6mm2, adj f0,f335,f345,f347
  f347: plane 2.42x1.93mm, normal (0,0,1), area 1.4mm2, adj f335,f336,f337,f338,f339,f340,f341,f342
  f348: plane 0.86x0.5mm, normal (0,-1,0), area 0.4mm2, adj f0,f349,f351,f352
  f349: plane 0.5x0.12mm, normal (1,0,0), area 0.1mm2, adj f0,f348,f350,f352
  f350: plane 0.86x0.5mm, normal (0,1,0), area 0.4mm2, adj f0,f349,f351,f352
  f351: plane 0.5x0.12mm, normal (-1,0,0), area 0.1mm2, adj f0,f348,f350,f352
  f352: plane 0.86x0.12mm, normal (0,0,1), area 0.1mm2, adj f348,f349,f350,f351
PLACE A t=(0.01,36.56,12.57)mm
PLACE B t=(0.01,36.65,32.57)mm
MATE fastened A.f4 <-> B.f1  axis (0,0,-1) through (0.01,51.65,32.57)mm
